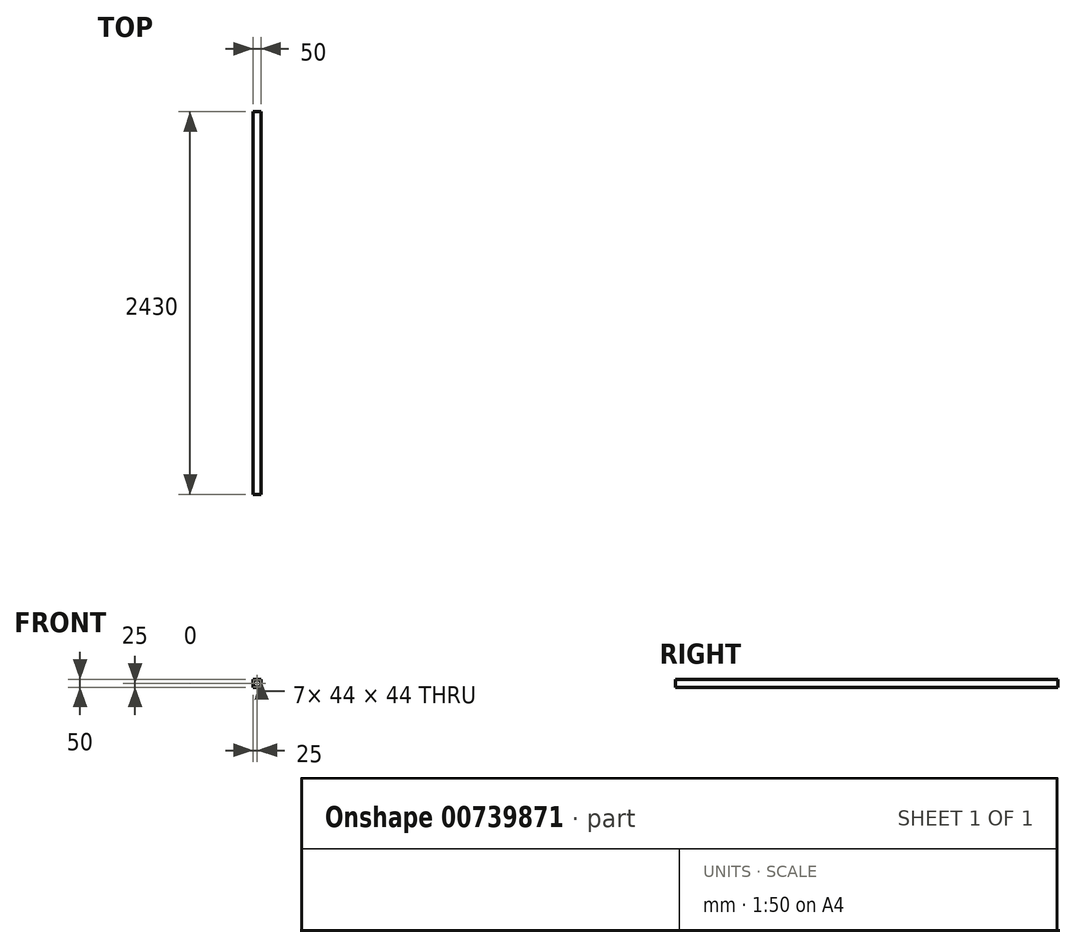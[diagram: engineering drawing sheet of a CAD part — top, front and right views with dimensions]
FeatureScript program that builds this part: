
annotation { "Feature Type Name" : "Feature", "Feature Type Description" : "" }
export const myFeature = defineFeature(function(context is Context, id is Id, definition is map)
    precondition{}
    {
        {
            var Q0;
            Q0=qCreatedBy(makeId("Front.planeOp"),FACE);
            var sketch = newSketch(context, id + "F0", { "sketchPlane" : qUnion([Q0])});
            skLineSegment(sketch, "E0.bottom", {"start": v(25, -25) * mm, "end": v(-25, -25) * mm});
            skLineSegment(sketch, "E0.top", {"start": v(25, 25) * mm, "end": v(-25, 25) * mm});
            skLineSegment(sketch, "E0.left", {"start": v(25, -25) * mm, "end": v(25, 25) * mm});
            skLineSegment(sketch, "E0.right", {"start": v(-25, -25) * mm, "end": v(-25, 25) * mm});
            skPoint(sketch, "E0.middle", {"position": v(0, 0) * mm});
            skLineSegment(sketch, "E1.0", {"start": v(22, 22) * mm, "end": v(-22, 22) * mm});
            skLineSegment(sketch, "E1.1", {"start": v(22, -22) * mm, "end": v(22, 22) * mm});
            skLineSegment(sketch, "E1.2", {"start": v(22, -22) * mm, "end": v(-22, -22) * mm});
            skLineSegment(sketch, "E1.3", {"start": v(-22, -22) * mm, "end": v(-22, 22) * mm});
            skSolve(sketch);
        }
        {
            var Q0;
            Q0=makeQuery(id+"F0.imprint","IMPRINT",FACE,{"disambiguationData":[TD([[makeQuery(id+"F0.imprint","IMPRINT",EDGE,{"derivedFrom":sQuery(id+"F0.wireOp",EDGE,"E0.bottom")}),-1.0]])]});
            extrude(context, id + "F1", {"entities" : qUnion([Q0]), "depth" : 2430 * mm, "offsetDistance" : 25 * mm});
        }
    });
